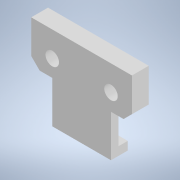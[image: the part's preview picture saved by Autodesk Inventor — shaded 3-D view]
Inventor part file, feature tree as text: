
AUTODESK INVENTOR PART (.ipt)
format: ipt  version: 2021 (Build 250183000, 183)  size: 124,928 bytes
history: native  units: mm
features: extrude x2, sketch x2, chamfer x1
ambient origin geometry x8: Origin, YZ Plane, XZ Plane, XY Plane, X Axis, Y Axis, Z Axis, Center Point
bodies: Solid1 (feature_tree)
feature tree (5):
  extrude  "Extrusion1"  Depth=14.0mm
  extrude  "Extrusion2"  Depth=10.0mm
  chamfer  "Chamfer1"  Distance=24.0mm
  sketch  "Sketch1"  dims[d0=14.0mm d1=6.0mm]
  sketch  "Sketch2"  dims[d2=14.0mm d3=10.0mm d4=24.0mm d5=3.2mm d6=7.0mm d7=4.0mm d8=0.0mm d9=4.0mm d10=2.2mm d11=8.0mm d12=2.0mm d13=0.0mm d14=0.0mm d15=2.0mm d16=2.0mm d17=45.0deg]
